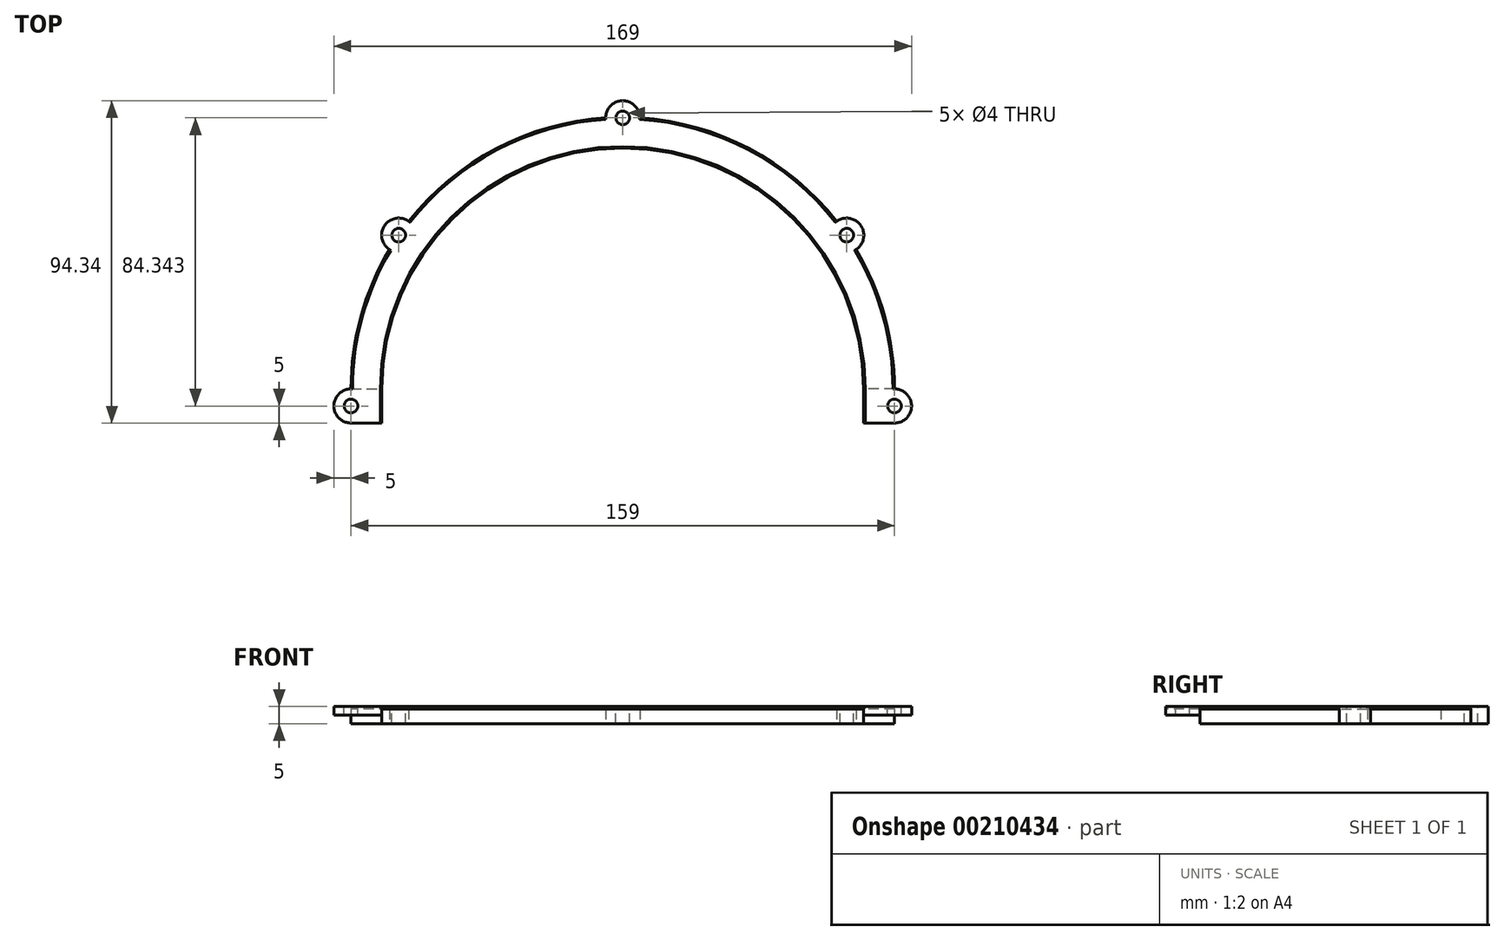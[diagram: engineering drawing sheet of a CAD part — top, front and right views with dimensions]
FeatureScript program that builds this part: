
annotation { "Feature Type Name" : "Feature", "Feature Type Description" : "" }
export const myFeature = defineFeature(function(context is Context, id is Id, definition is map)
    precondition{}
    {
        {
            var Q0;
            Q0=qCreatedBy(makeId("Top.planeOp"),FACE);
            var sketch = newSketch(context, id + "F0", { "sketchPlane" : qUnion([Q0])});
            skArc(sketch, "E0", {"start": v(79.5, 0) * mm, "mid": v(0, 79.5) * mm, "end": v(-79.5, 0) * mm});
            skArc(sketch, "E1", {"start": v(70.5, 0) * mm, "mid": v(0, 70.5) * mm, "end": v(-70.5, 0) * mm});
            skLineSegment(sketch, "E2", {"start": v(-79.5, 0) * mm, "end": v(-79.5, -10) * mm});
            skLineSegment(sketch, "E3", {"start": v(-70.5, 0) * mm, "end": v(-70.5, -10) * mm});
            skLineSegment(sketch, "E4", {"start": v(79.5, 0) * mm, "end": v(79.5, -10) * mm});
            skLineSegment(sketch, "E5", {"start": v(70.5, 0) * mm, "end": v(70.5, -10) * mm});
            skLineSegment(sketch, "E6", {"start": v(79.5, -35) * mm, "end": v(70.5, -35) * mm});
            skArc(sketch, "E7", {"start": v(5, 79.34) * mm, "mid": v(0, 84.34) * mm, "end": v(-5, 79.34) * mm});
            skArc(sketch, "E8", {"start": v(5, 79.34) * mm, "mid": v(0, 79.5) * mm, "end": v(-5, 79.34) * mm});
            skArc(sketch, "E9", {"start": v(-62.58, 49.03) * mm, "mid": v(-69.66, 47.83) * mm, "end": v(-68.24, 40.8) * mm});
            skArc(sketch, "E10", {"start": v(68.24, 40.8) * mm, "mid": v(69.66, 47.83) * mm, "end": v(62.58, 49.03) * mm});
            skArc(sketch, "E11", {"start": v(-79.5, 0) * mm, "mid": v(-84.5, -5) * mm, "end": v(-79.5, -10) * mm});
            skLineSegment(sketch, "E12", {"start": v(-79.5, -10) * mm, "end": v(-70.5, -10) * mm});
            skArc(sketch, "E13", {"start": v(79.5, -10) * mm, "mid": v(84.5, -5) * mm, "end": v(79.5, 0) * mm});
            skLineSegment(sketch, "E14", {"start": v(79.5, -10) * mm, "end": v(70.5, -10) * mm});
            skSolve(sketch);
        }
        {
            var Q0;
            Q0 = qSketchRegion(id + "F0", true);
            extrude(context, id + "F1", {"entities" : qUnion([Q0]), "depth" : 5 * mm});
        }
        {
            var Q0;
            Q0=makeQuery(id+"F1.opExtrude","CAP_FACE",FACE,{"disambiguationData":[OSD([sQuery(id+"F0.wireOp",EDGE,"E0"),sQuery(id+"F0.wireOp",EDGE,"E1"),sQuery(id+"F0.wireOp",EDGE,"E2"),sQuery(id+"F0.wireOp",EDGE,"cDQeXZSd-LWny-ZDhL-kl05-eoD5HqxgIg3F"),sQuery(id+"F0.wireOp",EDGE,"E3"),sQuery(id+"F0.wireOp",EDGE,"E4"),sQuery(id+"F0.wireOp",EDGE,"E5"),sQuery(id+"F0.wireOp",EDGE,"E6"),sQuery(id+"F0.wireOp",EDGE,"E7"),sQuery(id+"F0.wireOp",EDGE,"E9"),sQuery(id+"F0.wireOp",EDGE,"E10"),sQuery(id+"F0.wireOp",EDGE,"GLO6tf9o-7tT0-yfPW-c3aw-aKcGqFCE0EKz"),sQuery(id+"F0.wireOp",EDGE,"9xxhsYru-pBTT-gNjv-ujPh-2tLgfApbKMV2"),sQuery(id+"F0.wireOp",EDGE,"L5nhrC7s-5WGM-lfc8-sl2r-4DBKuFlaOpwm"),sQuery(id+"F0.wireOp",EDGE,"UQkAbaC7-vUoa-qm7U-ZzYs-JKjGYuxxddn5")])],"isStart":false});
            var sketch = newSketch(context, id + "F2", { "sketchPlane" : qUnion([Q0])});
            skCircle(sketch, "E15", {"center": v(0, 79.34) * mm, "radius": 2 * mm});
            skCircle(sketch, "E16", {"center": v(-65.54, 45) * mm, "radius": 2 * mm});
            skCircle(sketch, "E17", {"center": v(65.54, 45) * mm, "radius": 2 * mm});
            skCircle(sketch, "E18", {"center": v(-79.5, -5) * mm, "radius": 2 * mm});
            skCircle(sketch, "E19", {"center": v(79.5, -5) * mm, "radius": 2 * mm});
            skSolve(sketch);
        }
        {
            var Q0;
            Q0 = qSketchRegion(id + "F2", true);
            extrude(context, id + "F3", {"entities" : qUnion([Q0]), "operationType" : NewBodyOperationType.REMOVE, "oppositeDirection" : true, "depth" : 25 * mm});
        }
        {
            var Q0;
            Q0=makeQuery(id+"F1.opExtrude","CAP_EDGE",EDGE,{"disambiguationData":[OSD([sQuery(id+"F0.wireOp",EDGE,"E1")])],"isStart":false});
            var Q1;
            {var subQ0=sQuery(id+"F0.wireOp",EDGE,"E0");Q1=makeQuery(id+"F1.opExtrude","CAP_EDGE",EDGE,{"disambiguationData":[OSD([subQ0]),TDD([makeQuery(id+"F0.imprint","IMPRINT",EDGE,{"disambiguationData":[TD([[makeQuery(id+"F0.imprint","INTERSECT",VERTEX,{"disambiguationData":[OD(0.0)],"derivedFrom":[subQ0,sQuery(id+"F0.wireOp",EDGE,"E9")]}),1.0]])],"derivedFrom":subQ0})])],"isStart":false});}
            var Q2;
            {var subQ0=sQuery(id+"F0.wireOp",EDGE,"E0");Q2=makeQuery(id+"F1.opExtrude","CAP_EDGE",EDGE,{"disambiguationData":[OSD([subQ0]),TDD([makeQuery(id+"F0.imprint","IMPRINT",EDGE,{"disambiguationData":[TD([[makeQuery(id+"F0.imprint","INTERSECT",VERTEX,{"disambiguationData":[OD(1.0)],"derivedFrom":[subQ0,sQuery(id+"F0.wireOp",EDGE,"E10")]}),-1.0]])],"derivedFrom":subQ0})])],"isStart":false});}
            var Q3;
            {var subQ0=sQuery(id+"F0.wireOp",EDGE,"E0");Q3=makeQuery(id+"F1.opExtrude","CAP_EDGE",EDGE,{"disambiguationData":[OSD([subQ0]),TDD([makeQuery(id+"F0.imprint","IMPRINT",EDGE,{"disambiguationData":[TD([[makeQuery(id+"F0.imprint","INTERSECT",VERTEX,{"derivedFrom":[subQ0,sQuery(id+"F0.wireOp",EDGE,"E4")]}),-1.0]])],"derivedFrom":subQ0})])],"isStart":false});}
            var Q4;
            {var subQ0=sQuery(id+"F0.wireOp",EDGE,"E0");Q4=makeQuery(id+"F1.opExtrude","CAP_EDGE",EDGE,{"disambiguationData":[OSD([subQ0]),TDD([makeQuery(id+"F0.imprint","IMPRINT",EDGE,{"disambiguationData":[TD([[makeQuery(id+"F0.imprint","INTERSECT",VERTEX,{"derivedFrom":[subQ0,sQuery(id+"F0.wireOp",EDGE,"E2")]}),1.0]])],"derivedFrom":subQ0})])],"isStart":false});}
            chamfer(context, id + "F4", {"entities" : qUnion([Q0, Q1, Q2, Q3, Q4]), "chamferType" : ChamferType.OFFSET_ANGLE, "width" : .75 * mm, "oppositeDirection" : false, "angle" : 30 * degree, "tangentPropagation" : true});
        }
        {
            var Q0;
            Q0=makeQuery(id+"F1.opExtrude","CAP_FACE",FACE,{"disambiguationData":[OSD([sQuery(id+"F0.wireOp",EDGE,"E0"),sQuery(id+"F0.wireOp",EDGE,"E1"),sQuery(id+"F0.wireOp",EDGE,"E3"),sQuery(id+"F0.wireOp",EDGE,"E5"),sQuery(id+"F0.wireOp",EDGE,"E7"),sQuery(id+"F0.wireOp",EDGE,"E9"),sQuery(id+"F0.wireOp",EDGE,"E10"),sQuery(id+"F0.wireOp",EDGE,"E11"),sQuery(id+"F0.wireOp",EDGE,"E12"),sQuery(id+"F0.wireOp",EDGE,"E13"),sQuery(id+"F0.wireOp",EDGE,"E14")])],"isStart":true});
            var sketch = newSketch(context, id + "F5", { "sketchPlane" : qUnion([Q0])});
            skLineSegment(sketch, "E20", {"start": v(-79.5, 0) * mm, "end": v(-70.5, 0) * mm});
            skLineSegment(sketch, "E21", {"start": v(-70.5, 0) * mm, "end": v(-70.5, 10) * mm});
            skLineSegment(sketch, "E22", {"start": v(-70.5, 10) * mm, "end": v(-79.5, 10) * mm});
            skArc(sketch, "E23", {"start": v(-79.5, 10) * mm, "mid": v(-84.5, 5) * mm, "end": v(-79.5, 0) * mm});
            skLineSegment(sketch, "E24", {"start": v(79.5, 0) * mm, "end": v(70.5, 0) * mm});
            skLineSegment(sketch, "E25", {"start": v(70.5, 0) * mm, "end": v(70.5, 10) * mm});
            skLineSegment(sketch, "E26", {"start": v(70.5, 10) * mm, "end": v(79.5, 10) * mm});
            skArc(sketch, "E27", {"start": v(79.5, 0) * mm, "mid": v(84.5, 5) * mm, "end": v(79.5, 10) * mm});
            skSolve(sketch);
        }
        {
            var Q0;
            Q0 = qSketchRegion(id + "F5", true);
            extrude(context, id + "F6", {"entities" : qUnion([Q0]), "operationType" : NewBodyOperationType.REMOVE, "oppositeDirection" : true, "depth" : 2.5 * mm});
        }
    });
